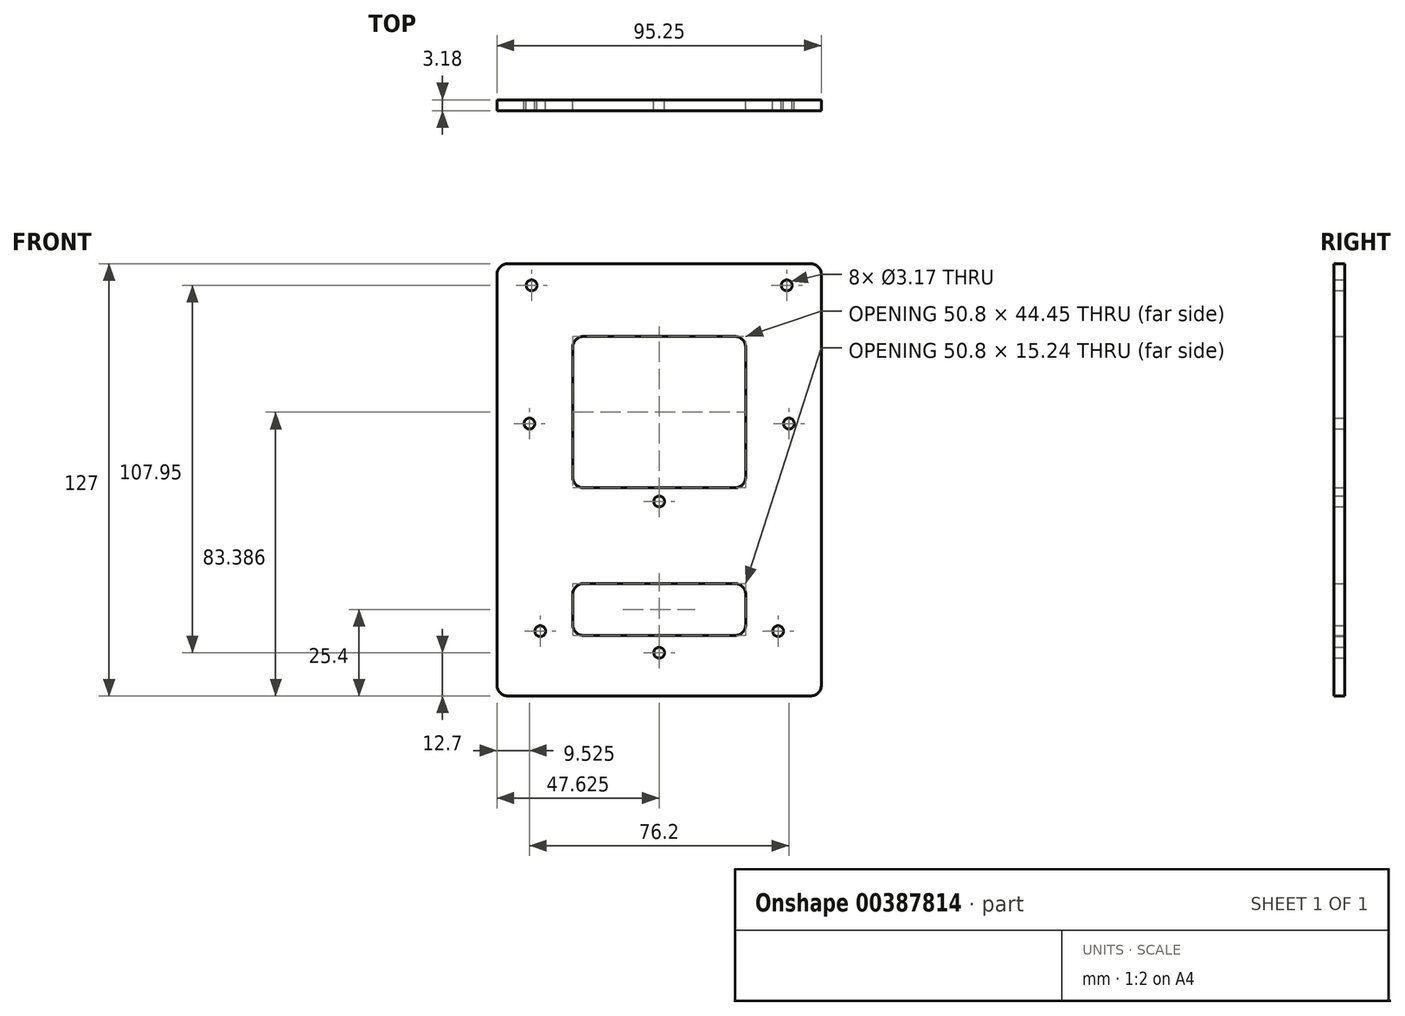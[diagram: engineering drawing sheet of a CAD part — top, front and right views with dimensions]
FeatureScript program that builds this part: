
annotation { "Feature Type Name" : "Feature", "Feature Type Description" : "" }
export const myFeature = defineFeature(function(context is Context, id is Id, definition is map)
    precondition{}
    {
        {
            var Q0;
            Q0=qCreatedBy(makeId("Front.planeOp"),FACE);
            var sketch = newSketch(context, id + "F0", { "sketchPlane" : qUnion([Q0])});
            skLineSegment(sketch, "E0.bottom", {"start": v(3.17, 0) * mm, "end": v(92.08, 0) * mm});
            skLineSegment(sketch, "E1.MirrorCS", {"start": v(0, -3.17) * mm, "end": v(0, -123.83) * mm});
            skLineSegment(sketch, "E2.MirrorCS", {"start": v(95.25, -3.17) * mm, "end": v(95.25, -123.83) * mm});
            skCircle(sketch, "E3.MirrorC", {"center": v(85.73, -46.95) * mm, "radius": 31.75 * mm, "construction": true});
            skCircle(sketch, "E4.MirrorC", {"center": v(47.63, -69.85) * mm, "radius": 31.75 * mm, "construction": true});
            skCircle(sketch, "E5.MirrorC", {"center": v(85.73, -46.95) * mm, "radius": 1.59 * mm});
            skLineSegment(sketch, "E6.MirrorCS", {"start": v(47.63, -127) * mm, "end": v(47.62, 0) * mm, "construction": true});
            skLineSegment(sketch, "E7.MirrorCS", {"start": v(3.17, -127) * mm, "end": v(92.08, -127) * mm});
            skCircle(sketch, "E8.MirrorC", {"center": v(9.52, -46.95) * mm, "radius": 1.59 * mm});
            skCircle(sketch, "E9.MirrorC", {"center": v(9.52, -46.95) * mm, "radius": 31.75 * mm, "construction": true});
            skCircle(sketch, "E10.MirrorC", {"center": v(47.63, -69.85) * mm, "radius": 1.59 * mm});
            skCircle(sketch, "E11.MirrorC", {"center": v(47.63, -69.85) * mm, "radius": 12.7 * mm, "construction": true});
            skCircle(sketch, "E12.MirrorC", {"center": v(47.62, -114.3) * mm, "radius": 12.7 * mm, "construction": true});
            skCircle(sketch, "E13.MirrorC", {"center": v(47.62, -114.3) * mm, "radius": 1.59 * mm});
            skCircle(sketch, "E14", {"center": v(10.16, -6.35) * mm, "radius": 1.59 * mm});
            skCircle(sketch, "E15", {"center": v(12.7, -107.95) * mm, "radius": 1.59 * mm});
            skCircle(sketch, "E16.MirrorC", {"center": v(82.55, -107.95) * mm, "radius": 1.59 * mm});
            skLineSegment(sketch, "E17.bottom", {"start": v(25.4, -21.39) * mm, "end": v(69.85, -21.39) * mm});
            skLineSegment(sketch, "E17.top", {"start": v(25.4, -65.84) * mm, "end": v(69.85, -65.84) * mm});
            skLineSegment(sketch, "E17.left", {"start": v(22.23, -24.56) * mm, "end": v(22.23, -62.66) * mm});
            skLineSegment(sketch, "E17.right", {"start": v(73.03, -24.56) * mm, "end": v(73.03, -62.66) * mm});
            skPoint(sketch, "E17.middle", {"position": v(47.63, -43.61) * mm});
            skLineSegment(sketch, "E18.bottom", {"start": v(69.85, -93.98) * mm, "end": v(25.4, -93.98) * mm});
            skLineSegment(sketch, "E18.top", {"start": v(69.85, -109.22) * mm, "end": v(25.4, -109.22) * mm});
            skLineSegment(sketch, "E18.left", {"start": v(73.03, -97.15) * mm, "end": v(73.03, -106.05) * mm});
            skLineSegment(sketch, "E18.right", {"start": v(22.23, -97.15) * mm, "end": v(22.23, -106.05) * mm});
            skPoint(sketch, "E18.middle", {"position": v(47.63, -101.6) * mm});
            skPoint(sketch, "E19.visualSharp", {"position": v(22.23, -21.39) * mm});
            skArc(sketch, "E19.filletArc", {"start": v(25.4, -21.39) * mm, "mid": v(23.15, -22.32) * mm, "end": v(22.23, -24.56) * mm});
            skPoint(sketch, "E20.visualSharp", {"position": v(73.03, -21.39) * mm});
            skArc(sketch, "E20.filletArc", {"start": v(73.03, -24.56) * mm, "mid": v(72.1, -22.32) * mm, "end": v(69.85, -21.39) * mm});
            skPoint(sketch, "E21.visualSharp", {"position": v(73.03, -65.84) * mm});
            skArc(sketch, "E21.filletArc", {"start": v(69.85, -65.84) * mm, "mid": v(72.1, -64.9) * mm, "end": v(73.03, -62.66) * mm});
            skPoint(sketch, "E22.visualSharp", {"position": v(22.23, -65.84) * mm});
            skArc(sketch, "E22.filletArc", {"start": v(22.23, -62.66) * mm, "mid": v(23.15, -64.9) * mm, "end": v(25.4, -65.84) * mm});
            skPoint(sketch, "E23.visualSharp", {"position": v(22.23, -93.98) * mm});
            skArc(sketch, "E23.filletArc", {"start": v(25.4, -93.98) * mm, "mid": v(23.15, -94.9) * mm, "end": v(22.23, -97.15) * mm});
            skPoint(sketch, "E24.visualSharp", {"position": v(73.03, -93.98) * mm});
            skArc(sketch, "E24.filletArc", {"start": v(73.02, -97.15) * mm, "mid": v(72.1, -94.9) * mm, "end": v(69.85, -93.98) * mm});
            skPoint(sketch, "E25.visualSharp", {"position": v(73.03, -109.22) * mm});
            skArc(sketch, "E25.filletArc", {"start": v(69.85, -109.22) * mm, "mid": v(72.1, -108.3) * mm, "end": v(73.02, -106.05) * mm});
            skPoint(sketch, "E26.visualSharp", {"position": v(22.23, -109.22) * mm});
            skArc(sketch, "E26.filletArc", {"start": v(22.23, -106.05) * mm, "mid": v(23.15, -108.3) * mm, "end": v(25.4, -109.22) * mm});
            skPoint(sketch, "E27.visualSharp", {"position": v(95.25, 0) * mm});
            skArc(sketch, "E27.filletArc", {"start": v(95.25, -3.17) * mm, "mid": v(94.32, -0.93) * mm, "end": v(92.08, 0) * mm});
            skPoint(sketch, "E28.visualSharp", {"position": v(0, 0) * mm});
            skArc(sketch, "E28.filletArc", {"start": v(3.17, 0) * mm, "mid": v(0.93, -0.93) * mm, "end": v(0, -3.17) * mm});
            skPoint(sketch, "E29.visualSharp", {"position": v(0, -127) * mm});
            skArc(sketch, "E29.filletArc", {"start": v(0, -123.83) * mm, "mid": v(0.93, -126.07) * mm, "end": v(3.17, -127) * mm});
            skPoint(sketch, "E30.visualSharp", {"position": v(95.25, -127) * mm});
            skArc(sketch, "E30.filletArc", {"start": v(92.08, -127) * mm, "mid": v(94.32, -126.07) * mm, "end": v(95.25, -123.83) * mm});
            skCircle(sketch, "E31.MirrorC", {"center": v(85.09, -6.35) * mm, "radius": 1.59 * mm});
            skSolve(sketch);
        }
        {
            var Q0;
            Q0 = qSketchRegion(id + "F0", true);
            extrude(context, id + "F1", {"entities" : qUnion([Q0]), "depth" : 3.17 * mm, "offsetDistance" : 25.4 * mm});
        }
    });
